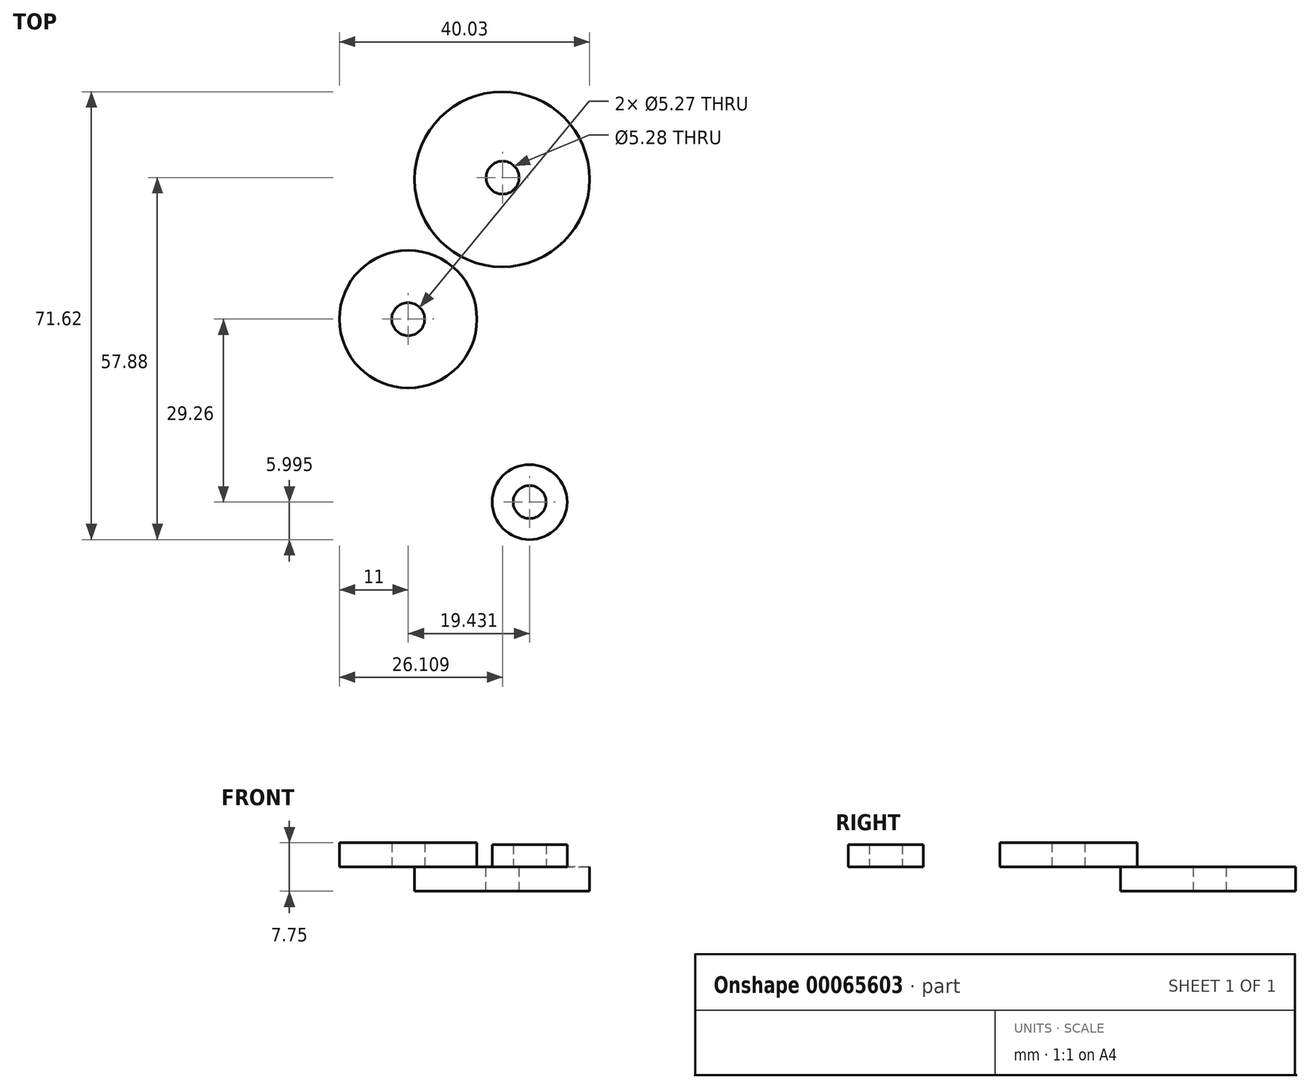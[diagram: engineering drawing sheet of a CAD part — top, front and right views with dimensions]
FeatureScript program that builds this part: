
annotation { "Feature Type Name" : "Feature", "Feature Type Description" : "" }
export const myFeature = defineFeature(function(context is Context, id is Id, definition is map)
    precondition{}
    {
        {
            var Q0;
            Q0=qCreatedBy(makeId("Top.planeOp"),FACE);
            var sketch = newSketch(context, id + "F0", { "sketchPlane" : qUnion([Q0])});
            skCircle(sketch, "E0", {"center": v(-39.89, 37.4) * mm, "radius": 14 * mm});
            skSolve(sketch);
        }
        {
            var Q0;
            Q0 = qSketchRegion(id + "F0", true);
            extrude(context, id + "F1", {"entities" : qUnion([Q0]), "oppositeDirection" : true, "depth" : 3.87 * mm});
        }
        {
            var Q0;
            Q0=qCreatedBy(makeId("Top.planeOp"),FACE);
            var sketch = newSketch(context, id + "F2", { "sketchPlane" : qUnion([Q0])});
            skPoint(sketch, "E1.endSnap0", {"position": v(-39.81, 37.66) * mm});
            skCircle(sketch, "E2", {"center": v(-39.81, 37.66) * mm, "radius": 2.64 * mm});
            skSolve(sketch);
        }
        {
            var Q0;
            Q0 = qSketchRegion(id + "F2", true);
            extrude(context, id + "F3", {"entities" : qUnion([Q0]), "operationType" : NewBodyOperationType.REMOVE, "oppositeDirection" : true, "depth" : 25 * mm});
        }
        {
            var Q0;
            Q0=qCreatedBy(makeId("Top.planeOp"),FACE);
            var sketch = newSketch(context, id + "F4", { "sketchPlane" : qUnion([Q0])});
            skCircle(sketch, "E3", {"center": v(-54.92, 15.04) * mm, "radius": 11 * mm});
            skCircle(sketch, "E4", {"center": v(-54.92, 15.04) * mm, "radius": 2.64 * mm});
            skSolve(sketch);
        }
        {
            var Q0;
            Q0 = qSketchRegion(id + "F4", true);
            extrude(context, id + "F5", {"entities" : qUnion([Q0]), "depth" : 3.88 * mm});
        }
        {
            var Q0;
            Q0=qCreatedBy(makeId("Top.planeOp"),FACE);
            var sketch = newSketch(context, id + "F6", { "sketchPlane" : qUnion([Q0])});
            skCircle(sketch, "E5", {"center": v(-35.49, -14.22) * mm, "radius": 6 * mm});
            skCircle(sketch, "E6", {"center": v(-35.49, -14.22) * mm, "radius": 2.64 * mm});
            skSolve(sketch);
        }
        {
            var Q0;
            Q0 = qSketchRegion(id + "F6", true);
            extrude(context, id + "F7", {"entities" : qUnion([Q0]), "depth" : 3.59 * mm});
        }
    });
